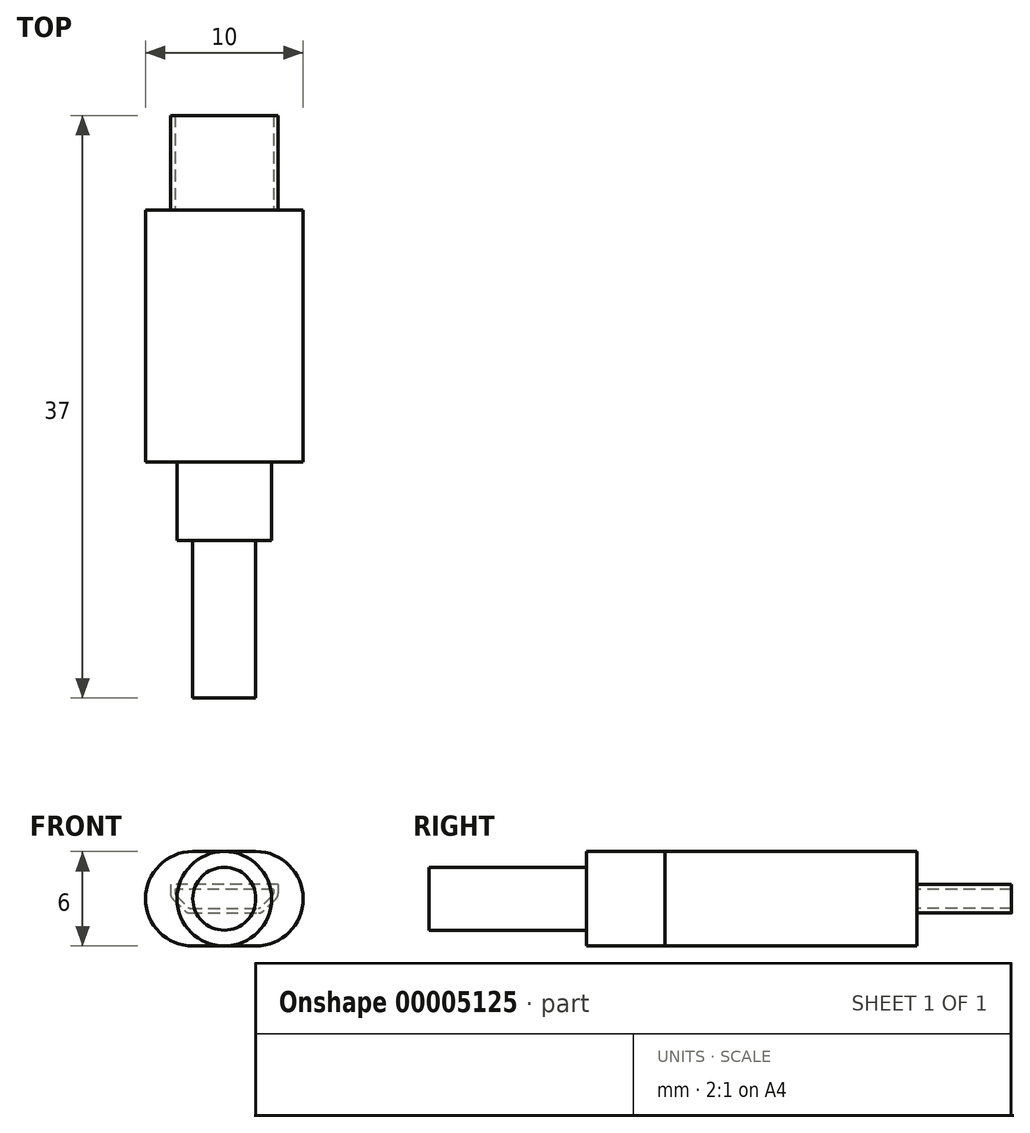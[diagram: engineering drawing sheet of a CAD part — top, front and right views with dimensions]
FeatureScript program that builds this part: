
annotation { "Feature Type Name" : "Feature", "Feature Type Description" : "" }
export const myFeature = defineFeature(function(context is Context, id is Id, definition is map)
    precondition{}
    {
        {
            var Q0;
            Q0=qCreatedBy(makeId("Top.planeOp"),FACE);
            var sketch = newSketch(context, id + "F0", { "sketchPlane" : qUnion([Q0])});
            skLineSegment(sketch, "E0.bottom", {"start": v(-5, 8) * mm, "end": v(-3.42, 8) * mm});
            skLineSegment(sketch, "E0.top", {"start": v(-5, -8) * mm, "end": v(5, -8) * mm});
            skLineSegment(sketch, "E0.left", {"start": v(-5, 8) * mm, "end": v(-5, -8) * mm});
            skLineSegment(sketch, "E0.right", {"start": v(5, 8) * mm, "end": v(5, -8) * mm});
            skLineSegment(sketch, "E1", {"start": v(0, 8) * mm, "end": v(0, -8) * mm, "construction": true});
            skLineSegment(sketch, "E2", {"start": v(-3.42, 8) * mm, "end": v(-3.42, 14) * mm});
            skLineSegment(sketch, "E3", {"start": v(-3.42, 14) * mm, "end": v(3.42, 14) * mm});
            skLineSegment(sketch, "E4", {"start": v(3.42, 14) * mm, "end": v(3.42, 8) * mm});
            skLineSegment(sketch, "E5", {"start": v(-3.42, 8) * mm, "end": v(3.42, 8) * mm});
            skLineSegment(sketch, "E6", {"start": v(3.42, 8) * mm, "end": v(5, 8) * mm});
            skSolve(sketch);
        }
        {
            var Q0;
            Q0=makeQuery(id+"F0.imprint","IMPRINT",FACE,{"disambiguationData":[TD([[makeQuery(id+"F0.imprint","IMPRINT",EDGE,{"derivedFrom":sQuery(id+"F0.wireOp",EDGE,"E0.bottom")}),-1.0]])]});
            extrude(context, id + "F1", {"entities" : qUnion([Q0]), "endBound" : BoundingType.SYMMETRIC, "depth" : 6 * mm});
        }
        {
            var Q0;
            Q0=makeQuery(id+"F1.opExtrude","SWEPT_FACE",FACE,{"disambiguationData":[OSD([sQuery(id+"F0.wireOp",EDGE,"E0.top")])]});
            var sketch = newSketch(context, id + "F2", { "sketchPlane" : qUnion([Q0])});
            skPoint(sketch, "E7.0", {"position": v(0, 0) * mm});
            skCircle(sketch, "E8", {"center": v(0, 0) * mm, "radius": 3 * mm});
            skCircle(sketch, "E9", {"center": v(0, 0) * mm, "radius": 2 * mm});
            skArc(sketch, "E10", {"start": v(-2, 3) * mm, "mid": v(-5, 0) * mm, "end": v(-2, -3) * mm});
            skArc(sketch, "E11", {"start": v(2, -3) * mm, "mid": v(5, 0) * mm, "end": v(2, 3) * mm});
            skLineSegment(sketch, "E12", {"start": v(-2, 3) * mm, "end": v(2, 3) * mm});
            skLineSegment(sketch, "E13", {"start": v(-2, -3) * mm, "end": v(2, -3) * mm});
            skSolve(sketch);
        }
        {
            var Q0;
            Q0=makeQuery(id+"F2.imprint","IMPRINT",FACE,{"disambiguationData":[TD([[makeQuery(id+"F2.imprint","IMPRINT",EDGE,{"derivedFrom":sQuery(id+"F2.wireOp",EDGE,"E9")}),-1.0]])]});
            extrude(context, id + "F3", {"entities" : qUnion([Q0]), "operationType" : NewBodyOperationType.ADD, "depth" : 5 * mm});
        }
        {
            var Q0;
            Q0=makeQuery(id+"F3.boolean.opBoolean","SPLIT",FACE,{"disambiguationData":[TD([makeQuery(id+"F3.opExtrude","SWEPT_FACE",FACE,{"disambiguationData":[OSD([sQuery(id+"F2.wireOp",EDGE,"E9")])]})])],"derivedFrom":makeQuery(id+"F1.opExtrude","SWEPT_FACE",FACE,{"disambiguationData":[OSD([sQuery(id+"F0.wireOp",EDGE,"E0.top")])]})});
            extrude(context, id + "F4", {"entities" : qUnion([Q0]), "operationType" : NewBodyOperationType.ADD, "depth" : 15 * mm});
        }
        {
            var Q0;
            {var subQ0=sQuery(id+"F0.wireOp",EDGE,"E0.top");var subQ1=makeQuery(id+"F1.opExtrude","CAP_EDGE",EDGE,{"disambiguationData":[OSD([subQ0])],"isStart":false});var subQ2=sQuery(id+"F2.wireOp",EDGE,"E11");var subQ3=makeQuery(id+"F2.imprint","INTERSECT",VERTEX,{"derivedFrom":[subQ1,subQ2,sQuery(id+"F2.wireOp",EDGE,"E12")]});Q0=makeQuery(id+"F2.imprint","IMPRINT",FACE,{"disambiguationData":[TD([[makeQuery(id+"F2.imprint","IMPRINT",EDGE,{"disambiguationData":[TD([[subQ3,1.0]])],"derivedFrom":subQ2}),-1.0]])]});}
            var Q1;
            {var subQ0=sQuery(id+"F0.wireOp",EDGE,"E0.top");var subQ1=makeQuery(id+"F1.opExtrude","CAP_EDGE",EDGE,{"disambiguationData":[OSD([subQ0])],"isStart":true});var subQ2=sQuery(id+"F2.wireOp",EDGE,"E11");var subQ3=makeQuery(id+"F2.imprint","INTERSECT",VERTEX,{"derivedFrom":[subQ1,subQ2,sQuery(id+"F2.wireOp",EDGE,"E13")]});Q1=makeQuery(id+"F2.imprint","IMPRINT",FACE,{"disambiguationData":[TD([[makeQuery(id+"F2.imprint","IMPRINT",EDGE,{"disambiguationData":[TD([[subQ3,-1.0]])],"derivedFrom":subQ2}),-1.0]])]});}
            var Q2;
            {var subQ0=sQuery(id+"F0.wireOp",EDGE,"E0.top");var subQ1=makeQuery(id+"F1.opExtrude","CAP_EDGE",EDGE,{"disambiguationData":[OSD([subQ0])],"isStart":false});var subQ2=sQuery(id+"F2.wireOp",EDGE,"E10");var subQ3=makeQuery(id+"F2.imprint","INTERSECT",VERTEX,{"derivedFrom":[subQ1,subQ2,sQuery(id+"F2.wireOp",EDGE,"E12")]});Q2=makeQuery(id+"F2.imprint","IMPRINT",FACE,{"disambiguationData":[TD([[makeQuery(id+"F2.imprint","IMPRINT",EDGE,{"disambiguationData":[TD([[subQ3,-1.0]])],"derivedFrom":subQ2}),-1.0]])]});}
            var Q3;
            {var subQ0=sQuery(id+"F0.wireOp",EDGE,"E0.top");var subQ1=makeQuery(id+"F1.opExtrude","CAP_EDGE",EDGE,{"disambiguationData":[OSD([subQ0])],"isStart":true});var subQ2=sQuery(id+"F2.wireOp",EDGE,"E10");var subQ3=makeQuery(id+"F2.imprint","INTERSECT",VERTEX,{"derivedFrom":[subQ1,subQ2,sQuery(id+"F2.wireOp",EDGE,"E13")]});Q3=makeQuery(id+"F2.imprint","IMPRINT",FACE,{"disambiguationData":[TD([[makeQuery(id+"F2.imprint","IMPRINT",EDGE,{"disambiguationData":[TD([[subQ3,1.0]])],"derivedFrom":subQ2}),-1.0]])]});}
            extrude(context, id + "F5", {"entities" : qUnion([Q0, Q1, Q2, Q3]), "operationType" : NewBodyOperationType.REMOVE, "endBound" : BoundingType.UP_TO_NEXT, "oppositeDirection" : true, "depth" : 25 * mm});
        }
        {
            var Q0;
            Q0=makeQuery(id+"F1.opExtrude","SWEPT_FACE",FACE,{"disambiguationData":[OSD([sQuery(id+"F0.wireOp",EDGE,"E0.bottom"),sQuery(id+"F0.wireOp",EDGE,"E5"),sQuery(id+"F0.wireOp",EDGE,"E6")])]});
            var sketch = newSketch(context, id + "F6", { "sketchPlane" : qUnion([Q0])});
            skLineSegment(sketch, "E14", {"start": v(-3.43, 0.9) * mm, "end": v(3.43, 0.9) * mm});
            skLineSegment(sketch, "E15", {"start": v(3.43, 0.9) * mm, "end": v(3.43, 0.36) * mm});
            skLineSegment(sketch, "E16", {"start": v(3.28, 0) * mm, "end": v(2.52, -0.75) * mm});
            skLineSegment(sketch, "E17", {"start": v(2.17, -0.9) * mm, "end": v(-2.17, -0.9) * mm});
            skLineSegment(sketch, "E18", {"start": v(-3.43, 0.9) * mm, "end": v(-3.43, 0.36) * mm});
            skLineSegment(sketch, "E19", {"start": v(-3.28, 0) * mm, "end": v(-2.52, -0.75) * mm});
            skLineSegment(sketch, "E20", {"start": v(0, 0.9) * mm, "end": v(0, -0.9) * mm, "construction": true});
            skPoint(sketch, "E21.visualSharp", {"position": v(-3.43, 0.15) * mm});
            skArc(sketch, "E21.filletArc", {"start": v(-3.43, 0.36) * mm, "mid": v(-3.39, 0.17) * mm, "end": v(-3.28, 0) * mm});
            skPoint(sketch, "E22.visualSharp", {"position": v(-2.38, -0.9) * mm});
            skArc(sketch, "E22.filletArc", {"start": v(-2.52, -0.75) * mm, "mid": v(-2.36, -0.86) * mm, "end": v(-2.17, -0.9) * mm});
            skPoint(sketch, "E23.visualSharp", {"position": v(2.38, -0.9) * mm});
            skArc(sketch, "E23.filletArc", {"start": v(2.17, -0.9) * mm, "mid": v(2.36, -0.86) * mm, "end": v(2.52, -0.75) * mm});
            skPoint(sketch, "E24.visualSharp", {"position": v(3.43, 0.15) * mm});
            skArc(sketch, "E24.filletArc", {"start": v(3.28, 0) * mm, "mid": v(3.39, 0.17) * mm, "end": v(3.43, 0.36) * mm});
            skLineSegment(sketch, "E25.0", {"start": v(-3.12, 0.6) * mm, "end": v(-3.12, 0.36) * mm});
            skArc(sketch, "E25.1", {"start": v(-3.12, 0.36) * mm, "mid": v(-3.1, 0.28) * mm, "end": v(-3.07, 0.22) * mm});
            skLineSegment(sketch, "E25.2", {"start": v(-3.07, 0.22) * mm, "end": v(-2.3, -0.54) * mm});
            skArc(sketch, "E25.3", {"start": v(-2.3, -0.54) * mm, "mid": v(-2.24, -0.58) * mm, "end": v(-2.17, -0.6) * mm});
            skLineSegment(sketch, "E25.4", {"start": v(2.17, -0.6) * mm, "end": v(-2.17, -0.6) * mm});
            skLineSegment(sketch, "E25.5", {"start": v(-3.12, 0.6) * mm, "end": v(3.12, 0.6) * mm});
            skArc(sketch, "E25.6", {"start": v(2.17, -0.6) * mm, "mid": v(2.24, -0.58) * mm, "end": v(2.3, -0.54) * mm});
            skLineSegment(sketch, "E25.7", {"start": v(3.07, 0.22) * mm, "end": v(2.3, -0.54) * mm});
            skArc(sketch, "E25.8", {"start": v(3.07, 0.22) * mm, "mid": v(3.1, 0.28) * mm, "end": v(3.13, 0.36) * mm});
            skLineSegment(sketch, "E25.9", {"start": v(3.12, 0.6) * mm, "end": v(3.12, 0.36) * mm});
            skSolve(sketch);
        }
        {
            var Q0;
            Q0=makeQuery(id+"F6.imprint","IMPRINT",FACE,{"disambiguationData":[TD([[makeQuery(id+"F6.imprint","IMPRINT",EDGE,{"derivedFrom":sQuery(id+"F6.wireOp",EDGE,"E14")}),-1.0]])]});
            extrude(context, id + "F7", {"entities" : qUnion([Q0]), "operationType" : NewBodyOperationType.ADD, "depth" : 6 * mm});
        }
    });
